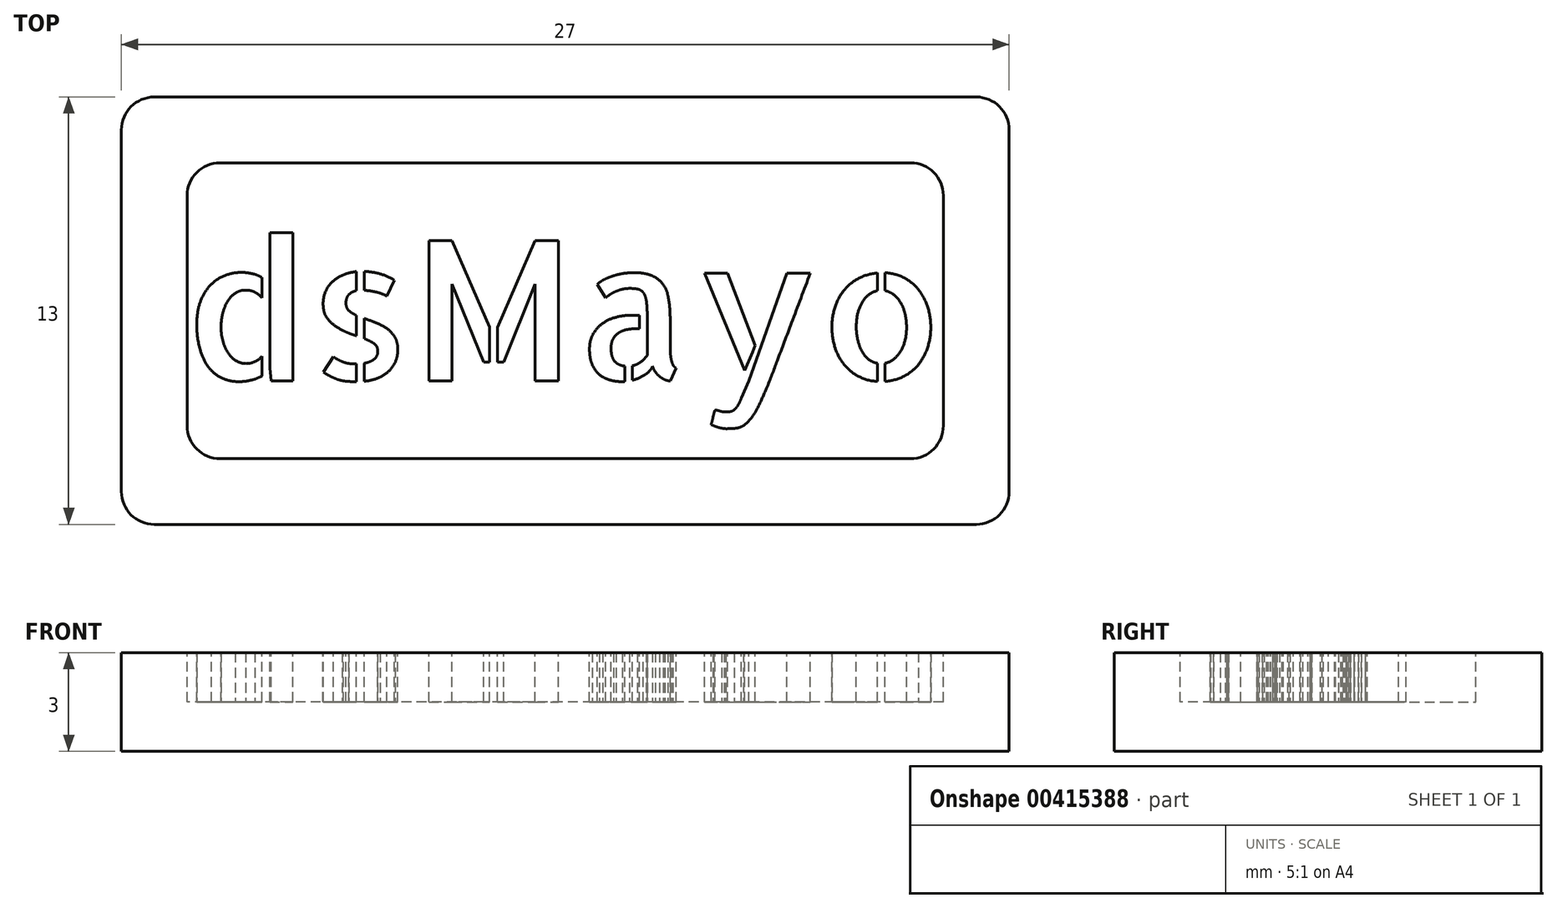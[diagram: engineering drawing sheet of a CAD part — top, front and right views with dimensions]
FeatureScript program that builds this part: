
annotation { "Feature Type Name" : "Feature", "Feature Type Description" : "" }
export const myFeature = defineFeature(function(context is Context, id is Id, definition is map)
    precondition{}
    {
        {
            var Q0;
            Q0=qCreatedBy(makeId("Top.planeOp"),FACE);
            var sketch = newSketch(context, id + "F0", { "sketchPlane" : qUnion([Q0])});
            skLineSegment(sketch, "E0.bottom", {"start": v(0, 0) * mm, "end": v(27, 0) * mm});
            skLineSegment(sketch, "E0.top", {"start": v(0, 13) * mm, "end": v(27, 13) * mm});
            skLineSegment(sketch, "E0.left", {"start": v(0, 0) * mm, "end": v(0, 13) * mm});
            skLineSegment(sketch, "E0.right", {"start": v(27, 0) * mm, "end": v(27, 13) * mm});
            skSolve(sketch);
        }
        {
            var Q0;
            Q0=makeQuery(id+"F0.imprint","IMPRINT",FACE,{"disambiguationData":[TD([[makeQuery(id+"F0.imprint","IMPRINT",EDGE,{"derivedFrom":sQuery(id+"F0.wireOp",EDGE,"E0.bottom")}),1.0]])]});
            extrude(context, id + "F1", {"entities" : qUnion([Q0]), "depth" : 3 * mm});
        }
        {
            var Q0;
            Q0=makeQuery(id+"F1.opExtrude","CAP_FACE",FACE,{"disambiguationData":[OSD([sQuery(id+"F0.wireOp",EDGE,"E0.bottom"),sQuery(id+"F0.wireOp",EDGE,"E0.top"),sQuery(id+"F0.wireOp",EDGE,"E0.left"),sQuery(id+"F0.wireOp",EDGE,"E0.right")])],"isStart":false});
            var sketch = newSketch(context, id + "F2", { "sketchPlane" : qUnion([Q0])});
            skLineSegment(sketch, "E1.0", {"start": v(24, 11) * mm, "end": v(3, 11) * mm});
            skLineSegment(sketch, "E1.1", {"start": v(25, 3) * mm, "end": v(25, 10) * mm});
            skLineSegment(sketch, "E1.2", {"start": v(3, 2) * mm, "end": v(24, 2) * mm});
            skLineSegment(sketch, "E1.3", {"start": v(2, 10) * mm, "end": v(2, 3) * mm});
            skText(sketch, "E2", { "text": "dsMayo", "fontName": "AllertaStencil-Regular.ttf"});
            skPoint(sketch, "E3.visualSharp", {"position": v(2, 11) * mm});
            skArc(sketch, "E3.filletArc", {"start": v(3, 11) * mm, "mid": v(2.3, 10.7) * mm, "end": v(2, 10) * mm});
            skPoint(sketch, "E4.visualSharp", {"position": v(25, 11) * mm});
            skArc(sketch, "E4.filletArc", {"start": v(25, 10) * mm, "mid": v(24.7, 10.7) * mm, "end": v(24, 11) * mm});
            skPoint(sketch, "E5.visualSharp", {"position": v(25, 2) * mm});
            skArc(sketch, "E5.filletArc", {"start": v(24, 2) * mm, "mid": v(24.7, 2.3) * mm, "end": v(25, 3) * mm});
            skPoint(sketch, "E6.visualSharp", {"position": v(2, 2) * mm});
            skArc(sketch, "E6.filletArc", {"start": v(2, 3) * mm, "mid": v(2.3, 2.3) * mm, "end": v(3, 2) * mm});
            const initialGuessF2  = {"E2": [0.002, 0.00437, 1, 0, 0.00427]};
            skSetInitialGuess(sketch, initialGuessF2);
            skSolve(sketch);
        }
        {
            var Q0;
            Q0=makeQuery(id+"F2.imprint","IMPRINT",FACE,{"disambiguationData":[TD([[makeQuery(id+"F2.imprint","IMPRINT",EDGE,{"derivedFrom":sQuery(id+"F2.wireOp",EDGE,"E1.0")}),1.0]])]});
            extrude(context, id + "F3", {"entities" : qUnion([Q0]), "operationType" : NewBodyOperationType.REMOVE, "oppositeDirection" : true, "depth" : 1.5 * mm});
        }
        {
            var Q0;
            Q0=makeQuery(id+"F1.opExtrude","SWEPT_EDGE",EDGE,{"disambiguationData":[OSD([sQuery(id+"F0.wireOp",EDGE,"E0.top"),sQuery(id+"F0.wireOp",EDGE,"E0.right")])]});
            var Q1;
            Q1=makeQuery(id+"F1.opExtrude","SWEPT_EDGE",EDGE,{"disambiguationData":[OSD([sQuery(id+"F0.wireOp",EDGE,"E0.bottom"),sQuery(id+"F0.wireOp",EDGE,"E0.right")])]});
            var Q2;
            Q2=makeQuery(id+"F1.opExtrude","SWEPT_EDGE",EDGE,{"disambiguationData":[OSD([sQuery(id+"F0.wireOp",EDGE,"E0.bottom"),sQuery(id+"F0.wireOp",EDGE,"E0.left")])]});
            var Q3;
            Q3=makeQuery(id+"F1.opExtrude","SWEPT_EDGE",EDGE,{"disambiguationData":[OSD([sQuery(id+"F0.wireOp",EDGE,"E0.top"),sQuery(id+"F0.wireOp",EDGE,"E0.left")])]});
            fillet(context, id + "F4", {"entities" : qUnion([Q0, Q1, Q2, Q3]), "radius" : 1 * mm, "tangentPropagation" : true, "allowEdgeOverflow" : false});
        }
    });
